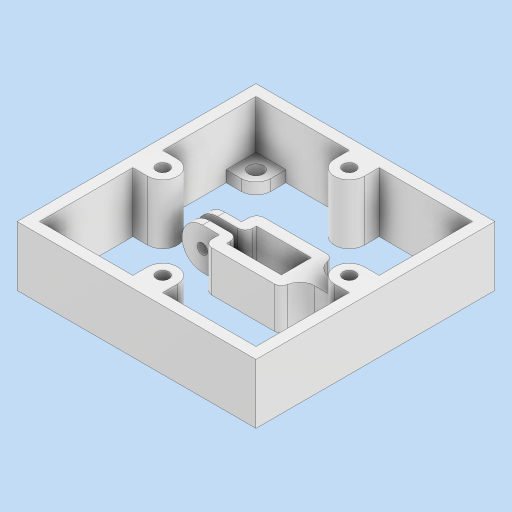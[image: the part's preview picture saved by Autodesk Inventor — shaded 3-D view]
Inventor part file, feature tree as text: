
AUTODESK INVENTOR PART (.ipt)
format: ipt  version: 2024 (Build 280153000, 153)  size: 427,520 bytes
history: native  units: in
note: dims shown in document units (in); Inventor stores cm internally (conversion verified against a paired STEP export)
features: sketch x5, extrude x4, fillet x3, pattern_circular x2, hole x2, projected_geometry x2
ambient origin geometry x8: Origin, YZ Plane, XZ Plane, XY Plane, X Axis, Y Axis, Z Axis, Center Point
bodies: Body1 (feature_tree)
feature tree (18):
  extrude  "Exterior Wall"  Depth=4.0in
  extrude  "Mounting Hole"  Depth=1.0in TaperAngle=0.0deg
  pattern_circular  "Mounting Hole Pattern"  [2 undecoded]
  extrude  "Servo Mount"  Depth=0.125in
  fillet  "Servo Mount Fillet 1"  Radius=0.1875in
  fillet  "Servo Mount Fillet 2"  Radius=1.5748in
  sketch  "Sketch18"  dims[d23=4.0in]
  extrude  "Cover Mounting Block"  Depth=0.5in
  hole  "Cover Mounting Hole"  [1 undecoded]
  pattern_circular  "Cover Mounting Pattern"  [2 undecoded]
  fillet  "Fillet15"  Radius=0.8996in
  hole  "Hole4"  [1 undecoded]
  sketch  "Sketch3"  dims[d17=4.0in d18=4.0in]
  sketch  "Sketch4"  dims[d19=0.1875in d20=1.0in d21=0.0in]
  sketch  "Sketch17"  dims[d22=4.0in]
  projected_geometry  "Projected Loop6"
  projected_geometry  "Projected Loop7"
  sketch  "Sketch19"  dims[d24=0.1875in d25=0.25in d26=0.125in d27=0.1875in d28=0.0in d30=1.5748in d31=360.0deg d125=0.1in d139=0.2323in d140=0.4843in d141=0.8996in d142=0.0079in d143=0.1875in d144=0.25in d145=0.6875in d146=0.0in d147=0.25in d148=0.125in d152=0.5in d153=1.0in d154=0.0in d155=0.21in d156=0.75in d157=0.315in d158=0.1181in d159=0.5635in d160=1.0in d161=0.8108in d162=1.5748in d163=360.0deg d165=0.125in d166=0.125in d167=0.8125in d168=0.3438in d169=0.175in d170=0.75in d171=0.375in d172=0.25in d173=0.5635in d174=1.0in d175=0.8108in d16=0.0312in d83=0.5in d84=0.0344in d85=0.5in d86=0.0344in]
note: 6 required parameter values undecoded (feature->parameter linkage not recoverable at this tier; creation-order binding heuristic only, values carry confidence <= 0.55)
